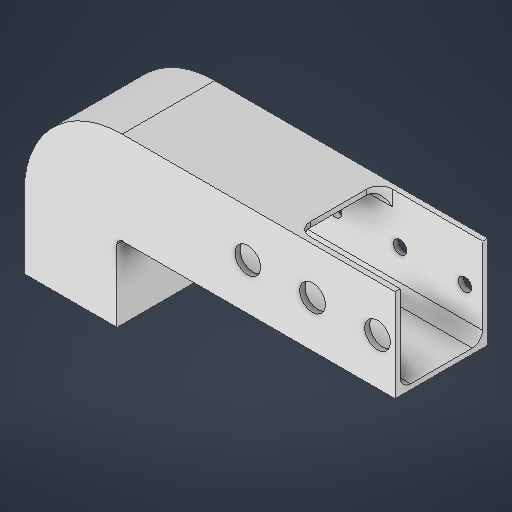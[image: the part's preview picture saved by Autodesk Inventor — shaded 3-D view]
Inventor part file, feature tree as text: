
AUTODESK INVENTOR PART (.ipt)
format: ipt  version: 2025.2 (Build 292293000, 293)  size: 354,816 bytes
history: native  units: in
note: dims shown in document units (in); Inventor stores cm internally (conversion verified against a paired STEP export)
features: fillet x9, extrude x6, sketch x5
ambient origin geometry x8: Origin, YZ Plane, XZ Plane, XY Plane, X Axis, Y Axis, Z Axis, Center Point
bodies: Solid1 (feature_tree)
feature tree (20):
  sketch  "Sketch1"  dims[d4=3.55in d5=1.6in]
  extrude  "Extrusion1"  Depth=1.6in
  extrude  "Extrusion2"  Depth=0.8in
  fillet  "Fillet1"  Radius=2.75in
  fillet  "Fillet2"  Radius=3.6in
  fillet  "Fillet3"  Radius=0.05in
  fillet  "Fillet4"  Radius=0.05in
  fillet  "Fillet5"  Radius=1.65in
  extrude  "Extrusion3"  Depth=2.7in
  extrude  "Extrusion4"  Depth=0.05in TaperAngle=0.0deg
  fillet  "Fillet6"  Radius=0.85in
  fillet  "Fillet7"  Radius=0.9in
  fillet  "Fillet8"  Radius=0.05in
  extrude  "Extrusion5"  Depth=0.125in
  extrude  "Extrusion6"  Depth=0.1in
  fillet  "Fillet9"  Radius=0.1299in
  sketch  "Sketch2"  dims[d6=0.8in d7=0.8in d8=2.75in d9=3.6in d10=0.05in d11=0.05in d12=1.65in]
  sketch  "Sketch3"  dims[d13=0.75in d14=2.7in]
  sketch  "Sketch4"  dims[d15=0.05in d16=0.05in d17=0.0in d18=0.85in d19=0.0in d20=0.9in d21=0.05in]
  sketch  "Sketch5"  dims[d22=0.1in d23=0.95in d24=0.1in d27=0.1299in d28=0.8in d29=0.1299in d30=0.1299in d31=0.45in d32=0.45in d33=0.45in d34=0.6299in d35=0.6299in d37=0.0in d38=0.0in d39=1.65in d41=2.7in d42=0.75in d43=0.05in d44=0.0in d45=0.05in d46=0.95in d47=0.1in d48=0.25in d49=0.25in d50=0.25in d51=0.45in d52=0.45in d53=0.45in d54=0.8in d55=0.6299in d56=0.6299in d57=0.0in d58=0.0in d59=1.0in d60=0.2in d61=0.0in d62=0.125in]
